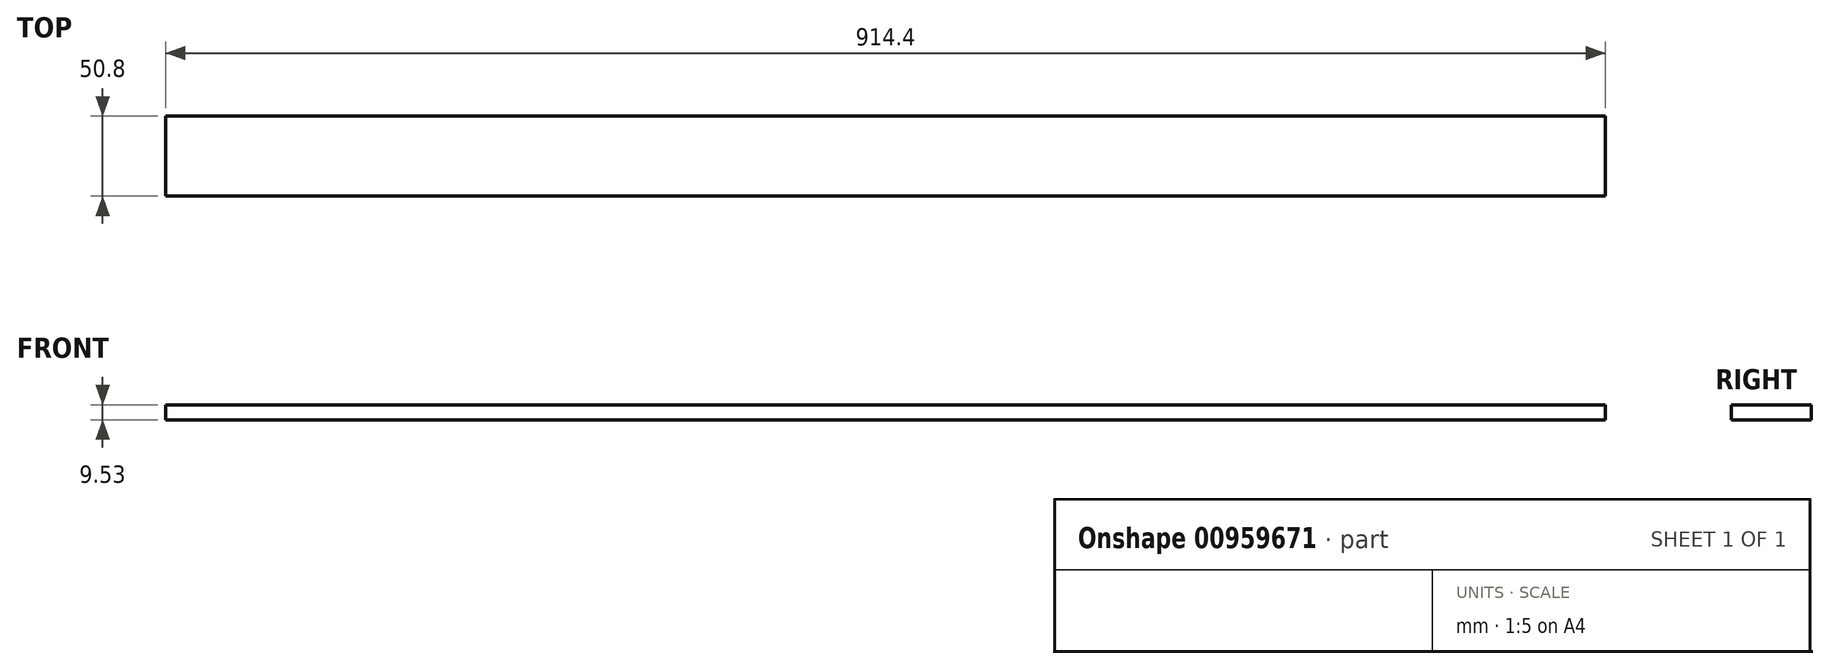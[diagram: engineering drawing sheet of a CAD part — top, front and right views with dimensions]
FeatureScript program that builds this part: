
annotation { "Feature Type Name" : "Feature", "Feature Type Description" : "" }
export const myFeature = defineFeature(function(context is Context, id is Id, definition is map)
    precondition{}
    {
        {
            var Q0;
            Q0=qCreatedBy(makeId("Top.planeOp"),FACE);
            var sketch = newSketch(context, id + "F0", { "sketchPlane" : qUnion([Q0])});
            skLineSegment(sketch, "E0.bottom", {"start": v(-57.4, 38.74) * mm, "end": v(857, 38.74) * mm});
            skLineSegment(sketch, "E0.top", {"start": v(-57.4, -12.06) * mm, "end": v(857, -12.06) * mm});
            skLineSegment(sketch, "E0.left", {"start": v(-57.4, 38.74) * mm, "end": v(-57.4, -12.06) * mm});
            skLineSegment(sketch, "E0.right", {"start": v(857, 38.74) * mm, "end": v(857, -12.06) * mm});
            skSolve(sketch);
        }
        {
            var Q0;
            Q0=makeQuery(id+"F0.imprint","IMPRINT",FACE,{"disambiguationData":[TD([[makeQuery(id+"F0.imprint","IMPRINT",EDGE,{"derivedFrom":sQuery(id+"F0.wireOp",EDGE,"E0.bottom")}),-1.0]])]});
            extrude(context, id + "F1", {"entities" : qUnion([Q0]), "depth" : 9.52 * mm, "offsetDistance" : 25.4 * mm});
        }
    });
